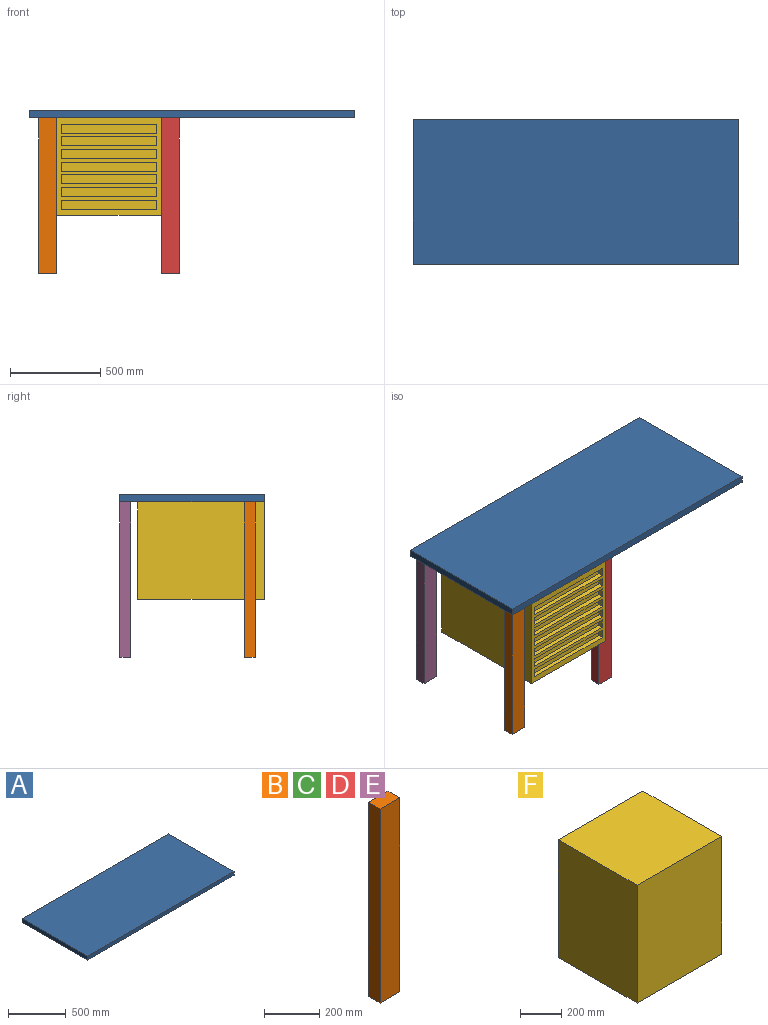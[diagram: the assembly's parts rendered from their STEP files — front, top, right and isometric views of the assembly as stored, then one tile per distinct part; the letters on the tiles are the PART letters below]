
ASSEMBLY  parts=6 mates=5
PART A: 6 faces, bbox 1800x800x40 mm
  f0: plane 1800x40mm, normal (0,-1,0), area 72000mm2, adj f1,f3,f4,f5
  f1: plane 800x40mm, normal (1,0,0), area 32000mm2, adj f0,f2,f4,f5
  f2: plane 1800x40mm, normal (0,1,0), area 72000mm2, adj f1,f3,f4,f5
  f3: plane 800x40mm, normal (-1,0,0), area 32000mm2, adj f0,f2,f4,f5
  f4: plane 1800x800mm, normal (0,0,1), area 1440000mm2, adj f0,f1,f2,f3
  f5: plane 1800x800mm, normal (0,0,-1), area 1440000mm2, adj f0,f1,f2,f3
PART B: 6 faces, bbox 100x60x860 mm
  f0: plane 860x100mm, normal (0,-1,0), area 86000mm2, adj f1,f3,f4,f5
  f1: plane 860x60mm, normal (1,0,0), area 51600mm2, adj f0,f2,f4,f5
  f2: plane 860x100mm, normal (0,1,0), area 86000mm2, adj f1,f3,f4,f5
  f3: plane 860x60mm, normal (-1,0,0), area 51600mm2, adj f0,f2,f4,f5
  f4: plane 100x60mm, normal (0,0,1), area 6000mm2, adj f0,f1,f2,f3
  f5: plane 100x60mm, normal (0,0,-1), area 6000mm2, adj f0,f1,f2,f3
PART C: same geometry as B
PART D: same geometry as B
PART E: same geometry as B
PART F: 41 faces, bbox 580x540x700 mm
  f0: plane 700x580mm, normal (0,1,0), area 406000mm2, adj f1,f2,f3,f4
  f1: plane 700x540mm, normal (1,0,0), area 378000mm2, adj f0,f2,f3,f5
  f2: plane 580x540mm, normal (0,0,-1), area 127700mm2, adj f0,f1,f4,f5,f6,f7,f8,f9
  f3: plane 580x540mm, normal (0,0,1), area 313200mm2, adj f0,f1,f4,f5
  f4: plane 700x540mm, normal (-1,0,0), area 378000mm2, adj f0,f2,f3,f5
  f5: plane 700x580mm, normal (0,-1,0), area 406000mm2, adj f1,f2,f3,f4
  f6: plane 530x25mm, normal (0,-1,0), area 13250mm2, adj f2,f7,f9,f10
  f7: plane 50x25mm, normal (-1,0,0), area 1250mm2, adj f2,f6,f8,f10
  f8: plane 530x25mm, normal (0,1,0), area 13250mm2, adj f2,f7,f9,f10
  f9: plane 50x25mm, normal (1,0,0), area 1250mm2, adj f2,f6,f8,f10
  f10: plane 530x50mm, normal (0,0,-1), area 26500mm2, adj f6,f7,f8,f9
  f11: plane 50x25mm, normal (1,0,0), area 1250mm2, adj f2,f12,f14,f15
  f12: plane 530x25mm, normal (0,-1,0), area 13250mm2, adj f2,f11,f13,f15
  f13: plane 50x25mm, normal (-1,0,0), area 1250mm2, adj f2,f12,f14,f15
  f14: plane 530x25mm, normal (0,1,0), area 13250mm2, adj f2,f11,f13,f15
  f15: plane 530x50mm, normal (0,0,-1), area 26500mm2, adj f11,f12,f13,f14
  f16: plane 530x25mm, normal (0,-1,0), area 13250mm2, adj f2,f17,f19,f20
  f17: plane 50x25mm, normal (-1,0,0), area 1250mm2, adj f2,f16,f18,f20
  f18: plane 530x25mm, normal (0,1,0), area 13250mm2, adj f2,f17,f19,f20
  f19: plane 50x25mm, normal (1,0,0), area 1250mm2, adj f2,f16,f18,f20
  f20: plane 530x50mm, normal (0,0,-1), area 26500mm2, adj f16,f17,f18,f19
  f21: plane 530x25mm, normal (0,-1,0), area 13250mm2, adj f2,f22,f24,f25
  f22: plane 50x25mm, normal (-1,0,0), area 1250mm2, adj f2,f21,f23,f25
  f23: plane 530x25mm, normal (0,1,0), area 13250mm2, adj f2,f22,f24,f25
  f24: plane 50x25mm, normal (1,0,0), area 1250mm2, adj f2,f21,f23,f25
  f25: plane 530x50mm, normal (0,0,-1), area 26500mm2, adj f21,f22,f23,f24
  f26: plane 530x25mm, normal (0,-1,0), area 13250mm2, adj f2,f27,f29,f30
  f27: plane 50x25mm, normal (-1,0,0), area 1250mm2, adj f2,f26,f28,f30
  f28: plane 530x25mm, normal (0,1,0), area 13250mm2, adj f2,f27,f29,f30
  f29: plane 50x25mm, normal (1,0,0), area 1250mm2, adj f2,f26,f28,f30
  f30: plane 530x50mm, normal (0,0,-1), area 26500mm2, adj f26,f27,f28,f29
  f31: plane 50x25mm, normal (1,0,0), area 1250mm2, adj f2,f32,f34,f35
  f32: plane 530x25mm, normal (0,-1,0), area 13250mm2, adj f2,f31,f33,f35
  f33: plane 50x25mm, normal (-1,0,0), area 1250mm2, adj f2,f32,f34,f35
  f34: plane 530x25mm, normal (0,1,0), area 13250mm2, adj f2,f31,f33,f35
  f35: plane 530x50mm, normal (0,0,-1), area 26500mm2, adj f31,f32,f33,f34
  f36: plane 50x25mm, normal (1,0,0), area 1250mm2, adj f2,f37,f39,f40
  f37: plane 530x25mm, normal (0,-1,0), area 13250mm2, adj f2,f36,f38,f40
  f38: plane 50x25mm, normal (-1,0,0), area 1250mm2, adj f2,f37,f39,f40
  f39: plane 530x25mm, normal (0,1,0), area 13250mm2, adj f2,f36,f38,f40
  f40: plane 530x50mm, normal (0,0,-1), area 26500mm2, adj f36,f37,f38,f39
PLACE A at identity fixed
PLACE B t=(-800,-320,-860)mm
PLACE C t=(-120,370,-860)mm
PLACE D t=(-120,-320,-860)mm
PLACE E t=(-800,370,-860)mm
PLACE F rot(axis=(0,-0.71,-0.71),180deg) t=(-460,300,-270)mm
MATE fastened E.f4 <-> A.f5  axis (0,0,1) through (-850,400,0)mm
MATE fastened F.f0 <-> A.f5  axis (0,0,1) through (-170,-400,0)mm
MATE fastened C.f4 <-> A.f5  axis (0,0,1) through (-70,340,0)mm
MATE fastened B.f4 <-> A.f5  axis (0,0,1) through (-850,-350,0)mm
MATE fastened D.f4 <-> A.f5  axis (0,0,1) through (-70,-350,0)mm
